# Revit family: LeL Metope 2.2
name_source: partatom
category: Lighting Fixtures
units: mm (PartAtom-declared; Revit-internal decimal feet)

## family parameters
Cut with Voids When Loaded = Yes
Host = Face
Light Source = No
Part Type = Normal
Room Calculation Point = No
Round Connector Dimension = Use Diameter
Shared = No

## types (12) — shared parameters
CCT = 3000 K
CRI = 80
Default Elevation = 1219 mm
Description = Outdoor Wall Mounted
Height = 60 mm  [stored 0.19685 ft]
IK = IK05
IP = IP65
Lamp = LED
Lenght = 35 mm  [stored 0.114829 ft]
Manufacturer = L&L Luce&Light
Model = TM22
URL = https://www.lucelight.it
Weight = 0.68 kg
Widht = 15 mm  [stored 0.0492126 ft]

## per-type parameters (varying)
| type | Alimentazione | Apparent Load | Lumen Output | Photometry1 | Photometry2 | Rated Power supply | Wattage |
| 2.2 DD 13W 24Vdc | 24 V | 13 VA | 920 lm | TM2 Light source : 2.2 D 7W 24Vdc | TM2 Light source : 2.2 D 7W 24Vdc | 24 V | 13 W |
| 2.2 DD 16W 230Vac | 230 V | 16 VA | 920 lm | TM2 Light source : 2.2 D 9W 110-230Vac | TM2 Light source : 2.2 D 9W 110-230Vac | 230 V | 16 W |
| 2.2 KK 52° 13W 24Vdc | 24 V | 13 VA | 1002 lm | TM2 Light source : 2.2 K 52° 7W 24Vdc | TM2 Light source : 2.2 K 52° 7W 24Vdc | 24 V | 13 W |
| 2.2 KK 52° 16W 230Vac | 230 V | 16 VA | 1002 lm | TM2 Light source : 2.2 K 52° 9W 110-230Vac | TM2 Light source : 2.2 K 52° 9W 110-230Vac | 230 V | 16 W |
| 2.2 LL 36° 13W 24Vdc | 24 V | 13 VA | 862 lm | TM2 Light source : 2.2 L 36° 7W 24Vdc | TM2 Light source : 2.2 L 36° 7W 24Vdc | 24 V | 13 W |
| 2.2 LL 36° 16W 230Vac | 230 V | 16 VA | 862 lm | TM2 Light source : 2.2 L 36° 9W 110-230Vac | TM2 Light source : 2.2 L 36° 9W 110-230Vac | 230 V | 16 W |
| 2.2 MM 26° 13W 24Vdc | 24 V | 13 VA | 938 lm | TM2 Light source : 2.2 M 26° 7W 24Vdc | TM2 Light source : 2.2 M 26° 7W 24Vdc | 24 V | 13 W |
| 2.2 MM 26° 16W 230Vac | 230 V | 16 VA | 938 lm | TM2 Light source : 2.2 M 26° 9W 110-230Vac | TM2 Light source : 2.2 M 26° 9W 110-230Vac | 230 V | 16 W |
| 2.2 SK 21°+52° 13W 24Vdc | 24 V | 13 VA | 969 lm | TM2 Light source : 2.2 S 21° 7W 24Vdc | TM2 Light source : 2.2 K 52° 7W 24Vdc | 24 V | 13 W |
| 2.2 SK 21°+52° 16W 230Vac | 230 V | 16 VA | 969 lm | TM2 Light source : 2.2 S 21° 9W 110-230Vac | TM2 Light source : 2.2 K 52° 9W 110-230Vac | 230 V | 16 W |
| 2.2 SS 21° 13W 24Vdc | 24 V | 13 VA | 938 lm | TM2 Light source : 2.2 S 21° 7W 24Vdc | TM2 Light source : 2.2 S 21° 7W 24Vdc | 24 V | 13 W |
| 2.2 SS 21° 16W 230Vac | 230 V | 16 VA | 938 lm | TM2 Light source : 2.2 S 21° 9W 110-230Vac | TM2 Light source : 2.2 S 21° 9W 110-230Vac | 230 V | 16 W |

note: [stored X ft] marks values corroborated as IEEE doubles in the binary element streams (Revit-internal decimal feet)
